# Revit family: Medical_Equipment-Workstation-Midmark_Medical-6215-Compact-Rectangular_Top-v1
name_source: partatom
category: Specialty Equipment
units: mm (PartAtom-declared; Revit-internal decimal feet)

## family parameters
Always vertical = Yes
Cut with Voids When Loaded = No
OmniClass Number = 23.40.70.11.14.11
OmniClass Title = Medical Equipment
Part Type = Normal
Room Calculation Point = No
Round Connector Dimension = Use Diameter
Shared = No
Work Plane-Based = No

## types (2) — shared parameters
Assembly Code = E1020800
Description = Flat Panel PC Workstation
Manufacturer = Midmark
Model = Midmark Medical 6215 Flat Panel PC Workstation - Rectangular - Compact
Product Documentation Link = https://www.midmark.com
Product Page URL = https://www.midmark.com
Product data url = https://bimobject.com
URL = https://www.midmark.com
Workstation Top Material = Wood - Midmark - Dark Walnut
zero-valued in all types: Cost

## type names (no varying parameters)
- 6215-002 - Rectangular Top
- 6215-002 - Spiro Workstation Top

## geometry (parser evidence)
native form markers: Blend x14, Sweep x25
no freeform markers — native parametric forms only
